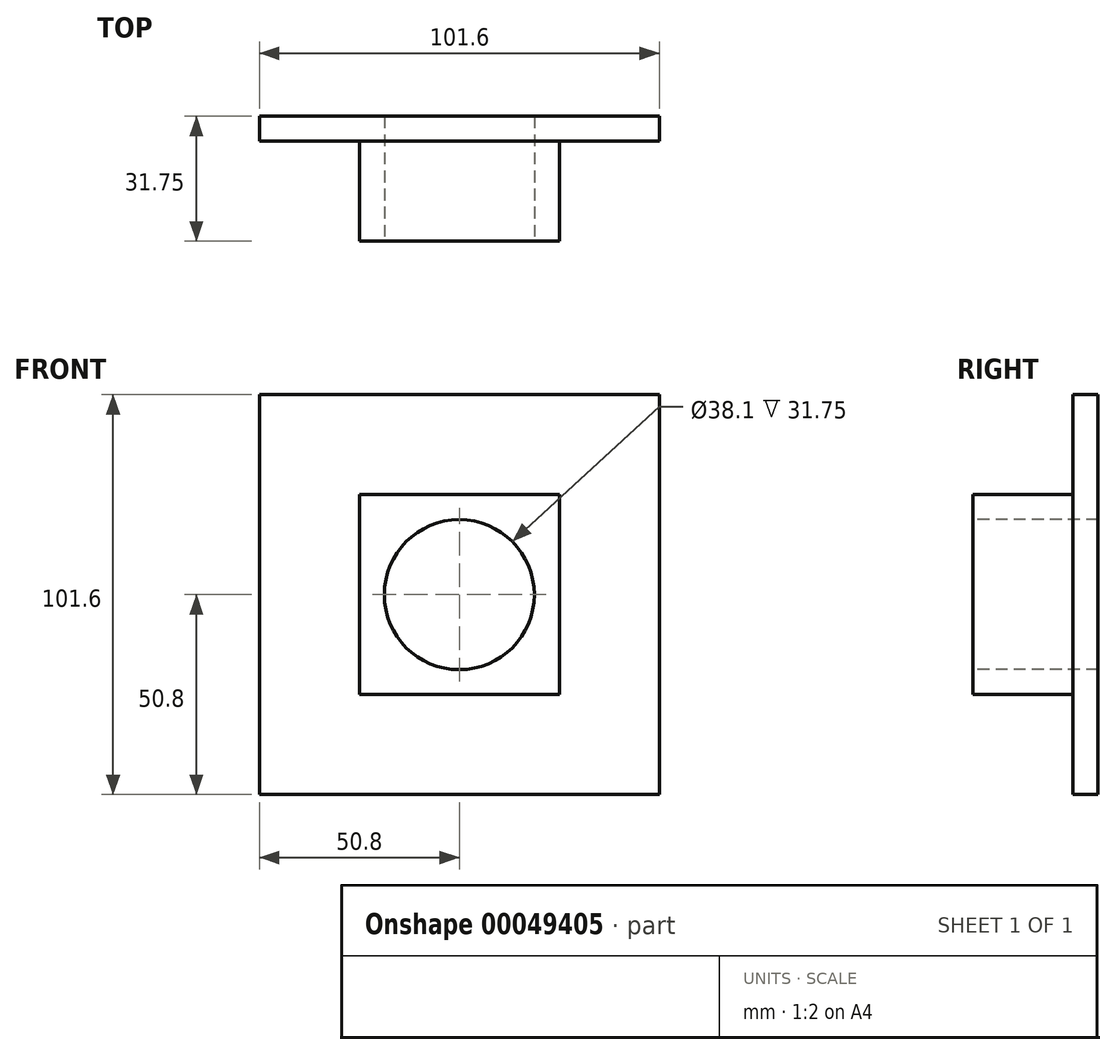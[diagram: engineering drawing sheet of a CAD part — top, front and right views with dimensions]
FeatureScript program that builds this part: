
annotation { "Feature Type Name" : "Feature", "Feature Type Description" : "" }
export const myFeature = defineFeature(function(context is Context, id is Id, definition is map)
    precondition{}
    {
        {
            var Q0;
            Q0=qCreatedBy(makeId("Front.planeOp"),FACE);
            var sketch = newSketch(context, id + "F0", { "sketchPlane" : qUnion([Q0])});
            skLineSegment(sketch, "E0.bottom", {"start": v(0, 0) * mm, "end": v(101.6, 0) * mm});
            skLineSegment(sketch, "E0.top", {"start": v(0, 101.6) * mm, "end": v(101.6, 101.6) * mm});
            skLineSegment(sketch, "E0.left", {"start": v(0, 0) * mm, "end": v(0, 101.6) * mm});
            skLineSegment(sketch, "E0.right", {"start": v(101.6, 0) * mm, "end": v(101.6, 101.6) * mm});
            skSolve(sketch);
        }
        {
            var Q0;
            Q0 = qSketchRegion(id + "F0", true);
            extrude(context, id + "F1", {"entities" : qUnion([Q0]), "depth" : 6.35 * mm});
        }
        {
            var Q0;
            Q0=makeQuery(id+"F1.opExtrude","CAP_FACE",FACE,{"disambiguationData":[OSD([sQuery(id+"F0.wireOp",EDGE,"E0.bottom"),sQuery(id+"F0.wireOp",EDGE,"E0.top"),sQuery(id+"F0.wireOp",EDGE,"E0.left"),sQuery(id+"F0.wireOp",EDGE,"E0.right")])],"isStart":false});
            var sketch = newSketch(context, id + "F2", { "sketchPlane" : qUnion([Q0])});
            skLineSegment(sketch, "E1.bottom", {"start": v(25.4, 76.2) * mm, "end": v(76.2, 76.2) * mm});
            skLineSegment(sketch, "E1.top", {"start": v(25.4, 25.4) * mm, "end": v(76.2, 25.4) * mm});
            skLineSegment(sketch, "E1.left", {"start": v(25.4, 76.2) * mm, "end": v(25.4, 25.4) * mm});
            skLineSegment(sketch, "E1.right", {"start": v(76.2, 76.2) * mm, "end": v(76.2, 25.4) * mm});
            skSolve(sketch);
        }
        {
            var Q0;
            Q0 = qSketchRegion(id + "F2", true);
            extrude(context, id + "F3", {"entities" : qUnion([Q0]), "operationType" : NewBodyOperationType.ADD, "depth" : 25.4 * mm});
        }
        {
            var Q0;
            Q0=makeQuery(id+"F3.opExtrude","CAP_FACE",FACE,{"disambiguationData":[OSD([sQuery(id+"F2.wireOp",EDGE,"E1.bottom"),sQuery(id+"F2.wireOp",EDGE,"E1.top"),sQuery(id+"F2.wireOp",EDGE,"E1.left"),sQuery(id+"F2.wireOp",EDGE,"E1.right")])],"isStart":false});
            var sketch = newSketch(context, id + "F4", { "sketchPlane" : qUnion([Q0])});
            skCircle(sketch, "E2", {"center": v(50.8, 50.8) * mm, "radius": 19.05 * mm});
            skSolve(sketch);
        }
        {
            var Q0;
            Q0 = qSketchRegion(id + "F4", true);
            extrude(context, id + "F5", {"entities" : qUnion([Q0]), "operationType" : NewBodyOperationType.REMOVE, "endBound" : BoundingType.THROUGH_ALL, "oppositeDirection" : true, "depth" : 25.4 * mm});
        }
    });
